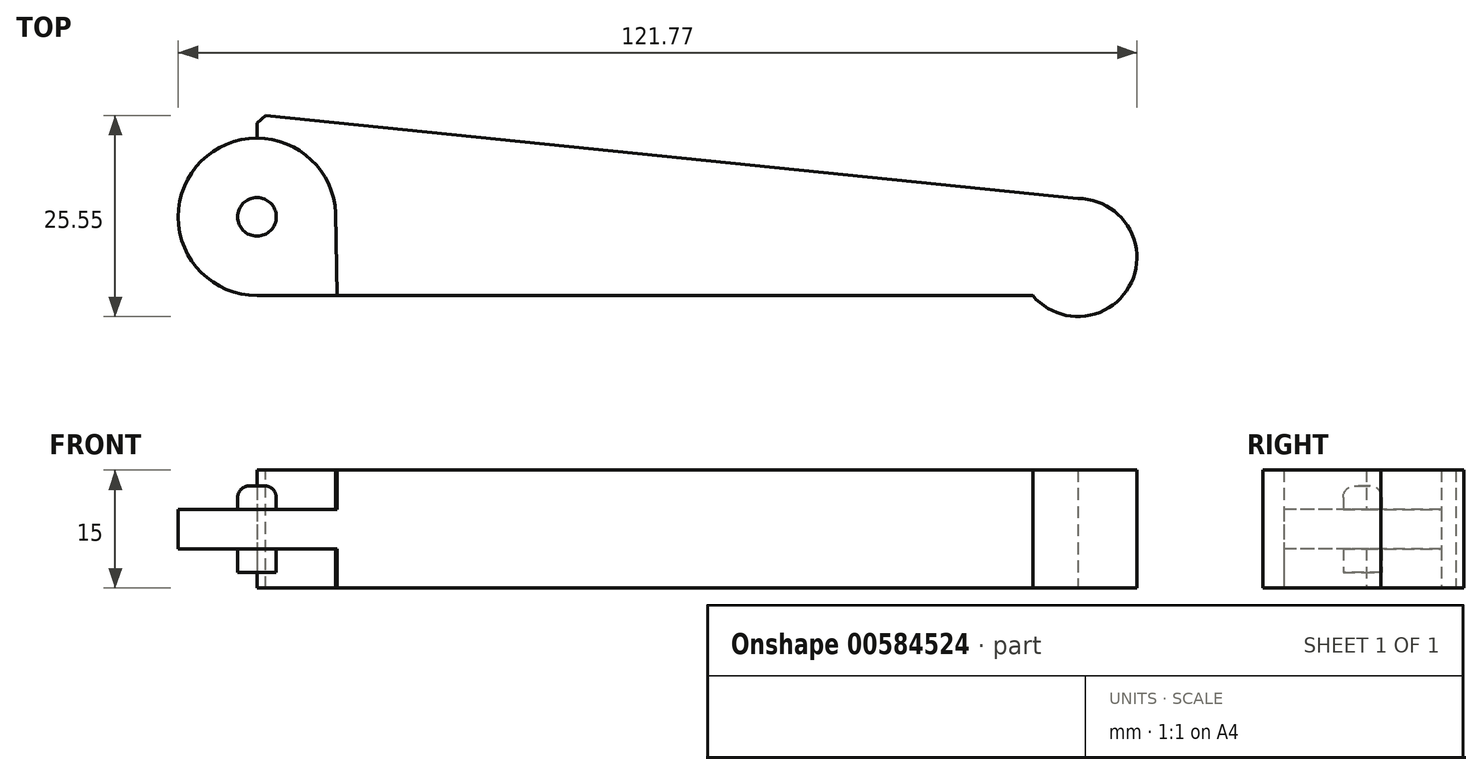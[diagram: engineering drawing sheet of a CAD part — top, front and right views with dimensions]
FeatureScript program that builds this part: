
annotation { "Feature Type Name" : "Feature", "Feature Type Description" : "" }
export const myFeature = defineFeature(function(context is Context, id is Id, definition is map)
    precondition{}
    {
        {
            var Q0;
            Q0=qCreatedBy(makeId("Top.planeOp"),FACE);
            var sketch = newSketch(context, id + "F0", { "sketchPlane" : qUnion([Q0])});
            skPoint(sketch, "E0.middle", {"position": v(0, 0) * mm});
            skLineSegment(sketch, "E1", {"start": v(7.55, 0) * mm, "end": v(106.1, 0) * mm});
            skArc(sketch, "E2", {"start": v(106.1, 0) * mm, "mid": v(118.62, 1.68) * mm, "end": v(111.82, 12.34) * mm});
            skArc(sketch, "E3", {"start": v(7.55, 20) * mm, "mid": v(-2.45, 10) * mm, "end": v(7.55, 0) * mm});
            skPoint(sketch, "E4.orphan", {"position": v(117.55, 0) * mm});
            skLineSegment(sketch, "E5", {"start": v(7.55, 20) * mm, "end": v(7.55, 23) * mm});
            skLineSegment(sketch, "E6", {"start": v(7.55, 23) * mm, "end": v(111.82, 12.34) * mm});
            skSolve(sketch);
        }
        {
            var Q0;
            Q0=qSketchRegion(id+"F0",true);
            extrude(context, id + "F1", {"entities" : qUnion([Q0]), "depth" : 15 * mm, "offsetDistance" : 25 * mm});
        }
        {
            var Q0;
            Q0=qCreatedBy(makeId("Top.planeOp"),FACE);
            var sketch = newSketch(context, id + "F2", { "sketchPlane" : qUnion([Q0])});
            skPoint(sketch, "E7.0", {"position": v(7.55, 10) * mm});
            skArc(sketch, "E8", {"start": v(17.54, 10.48) * mm, "mid": v(0.31, 16.9) * mm, "end": v(7.55, 0) * mm});
            skCircle(sketch, "E9", {"center": v(7.55, 10) * mm, "radius": 2.45 * mm});
            skLineSegment(sketch, "E10", {"start": v(17.54, 10.48) * mm, "end": v(17.72, 0) * mm});
            skLineSegment(sketch, "E11", {"start": v(17.72, 0) * mm, "end": v(7.55, 0) * mm});
            skSolve(sketch);
        }
        {
            var Q0;
            Q0=qSketchRegion(id+"F2",true);
            extrude(context, id + "F3", {"entities" : qUnion([Q0]), "operationType" : NewBodyOperationType.REMOVE, "depth" : 5 * mm, "offsetDistance" : 25 * mm});
        }
        {
            var Q0;
            Q0=qSketchRegion(id+"F2",true);
            extrude(context, id + "F4", {"entities" : qUnion([Q0]), "operationType" : NewBodyOperationType.REMOVE, "endBound" : BoundingType.UP_TO_NEXT, "depth" : 10 * mm, "hasOffset" : true, "offsetDistance" : 10 * mm, "offsetOppositeDirection" : true, "hasSecondDirection" : true, "secondDirectionOppositeDirection" : false, "secondDirectionDepth" : 10 * mm});
        }
        {
            var Q0;
            Q0=makeQuery(id+"F4.boolean.opBoolean","SPLIT",FACE,{"disambiguationData":[TD([makeQuery(id+"F4.opExtrude","SWEPT_FACE",FACE,{"disambiguationData":[OSD([sQuery(id+"F2.wireOp",EDGE,"E9")])]})])],"derivedFrom":makeQuery(id+"F1.opExtrude","CAP_FACE",FACE,{"disambiguationData":[OSD([sQuery(id+"F0.wireOp",EDGE,"E1"),sQuery(id+"F0.wireOp",EDGE,"E2"),sQuery(id+"F0.wireOp",EDGE,"E3"),sQuery(id+"F0.wireOp",EDGE,"ICITt8e3-zTpg-WYht-18EF-VDJriyI8qyvp"),sQuery(id+"F0.wireOp",EDGE,"QLlQdMzX-Z1Ki-qbhD-PUhB-xGOlY88uPTue")])],"isStart":false})});
            extrude(context, id + "F5", {"entities" : qUnion([Q0]), "operationType" : NewBodyOperationType.REMOVE, "oppositeDirection" : true, "depth" : 2 * mm, "offsetDistance" : 25 * mm});
        }
        {
            var Q0;
            Q0=makeQuery(id+"F3.boolean.opBoolean","SPLIT",FACE,{"disambiguationData":[TD([makeQuery(id+"F3.opExtrude","SWEPT_FACE",FACE,{"disambiguationData":[OSD([sQuery(id+"F2.wireOp",EDGE,"E9")])]})])],"derivedFrom":makeQuery(id+"F1.opExtrude","CAP_FACE",FACE,{"disambiguationData":[OSD([sQuery(id+"F0.wireOp",EDGE,"E1"),sQuery(id+"F0.wireOp",EDGE,"E2"),sQuery(id+"F0.wireOp",EDGE,"E3"),sQuery(id+"F0.wireOp",EDGE,"ICITt8e3-zTpg-WYht-18EF-VDJriyI8qyvp"),sQuery(id+"F0.wireOp",EDGE,"QLlQdMzX-Z1Ki-qbhD-PUhB-xGOlY88uPTue")])],"isStart":true})});
            extrude(context, id + "F6", {"entities" : qUnion([Q0]), "operationType" : NewBodyOperationType.REMOVE, "oppositeDirection" : true, "depth" : 2 * mm, "offsetDistance" : 25 * mm});
        }
        {
            var Q0;
            Q0=makeQuery(id+"F5.boolean.opBoolean","COPY",FACE,{"derivedFrom":makeQuery(id+"F5.opExtrude","CAP_FACE",FACE,{"disambiguationData":[OSD([sQuery(id+"F0.wireOp",EDGE,"E1"),sQuery(id+"F0.wireOp",EDGE,"E2"),sQuery(id+"F0.wireOp",EDGE,"E3"),sQuery(id+"F0.wireOp",EDGE,"ICITt8e3-zTpg-WYht-18EF-VDJriyI8qyvp"),sQuery(id+"F0.wireOp",EDGE,"QLlQdMzX-Z1Ki-qbhD-PUhB-xGOlY88uPTue")])],"isStart":false})});
            var Q1;
            Q1=makeQuery(id+"F6.boolean.opBoolean","COPY",EDGE,{"derivedFrom":makeQuery(id+"F6.opExtrude","CAP_EDGE",EDGE,{"disambiguationData":[OSD([sQuery(id+"F2.wireOp",EDGE,"E9")])],"isStart":false})});
            fillet(context, id + "F7", {"entities" : qUnion([Q0, Q1]), "radius" : 1.5 * mm, "tangentPropagation" : true, "allowEdgeOverflow" : false});
        }
        {
            var Q0;
            Q0=makeQuery(id+"F1.opExtrude","SWEPT_EDGE",EDGE,{"disambiguationData":[OSD([sQuery(id+"F0.wireOp",EDGE,"E5"),sQuery(id+"F0.wireOp",EDGE,"E6")])]});
            chamfer(context, id + "F8", {"entities" : qUnion([Q0]), "width" : 1 * mm, "tangentPropagation" : true});
        }
    });
